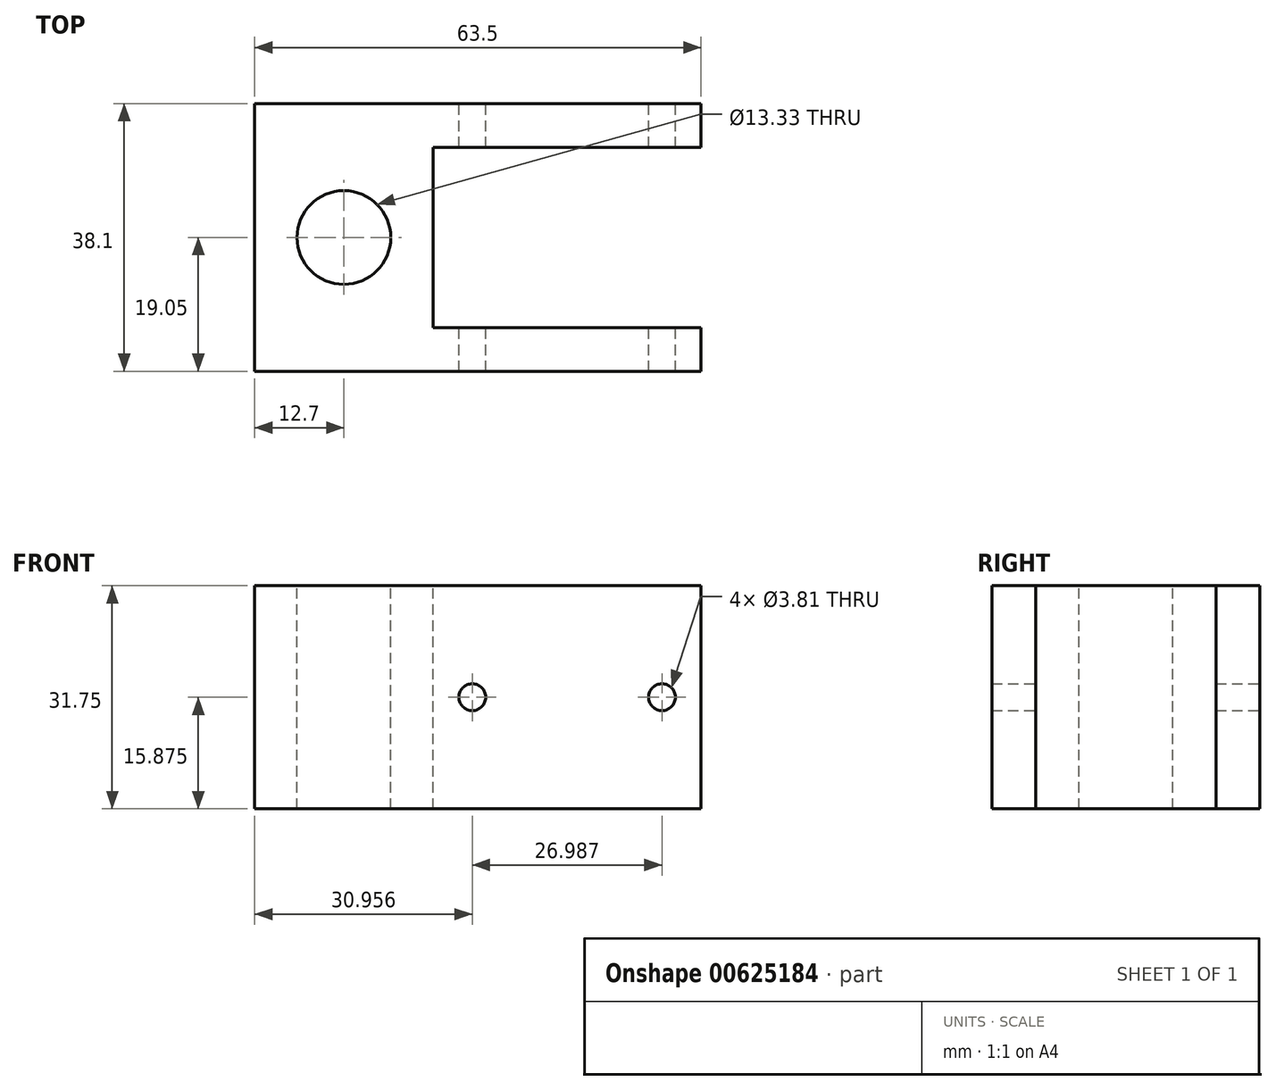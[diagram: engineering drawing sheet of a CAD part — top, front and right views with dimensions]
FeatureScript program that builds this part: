
annotation { "Feature Type Name" : "Feature", "Feature Type Description" : "" }
export const myFeature = defineFeature(function(context is Context, id is Id, definition is map)
    precondition{}
    {
        {
            var Q0;
            Q0=qCreatedBy(makeId("Top.planeOp"),FACE);
            var sketch = newSketch(context, id + "F0", { "sketchPlane" : qUnion([Q0])});
            skLineSegment(sketch, "E0.bottom", {"start": v(12.7, -19.05) * mm, "end": v(-12.7, -19.05) * mm});
            skLineSegment(sketch, "E0.top", {"start": v(12.7, 19.05) * mm, "end": v(-12.7, 19.05) * mm});
            skLineSegment(sketch, "E0.left", {"start": v(12.7, -19.05) * mm, "end": v(12.7, 19.05) * mm});
            skLineSegment(sketch, "E0.right", {"start": v(-12.7, -19.05) * mm, "end": v(-12.7, 19.05) * mm});
            skPoint(sketch, "E0.middle", {"position": v(0, 0) * mm});
            skSolve(sketch);
        }
        {
            var Q0;
            Q0=makeQuery(id+"F0.imprint","IMPRINT",FACE,{"disambiguationData":[TD([[makeQuery(id+"F0.imprint","IMPRINT",EDGE,{"derivedFrom":sQuery(id+"F0.wireOp",EDGE,"E0.bottom")}),-1.0]])]});
            extrude(context, id + "F1", {"entities" : qUnion([Q0]), "depth" : 31.75 * mm, "offsetDistance" : 25.4 * mm});
        }
        {
            var Q0;
            Q0=makeQuery(id+"F1.opExtrude","SWEPT_FACE",FACE,{"disambiguationData":[OSD([sQuery(id+"F0.wireOp",EDGE,"E0.left")])]});
            var sketch = newSketch(context, id + "F2", { "sketchPlane" : qUnion([Q0])});
            skLineSegment(sketch, "E1.bottom", {"start": v(-19.05, 0) * mm, "end": v(-12.83, 0) * mm});
            skLineSegment(sketch, "E1.top", {"start": v(-19.05, 31.75) * mm, "end": v(-12.83, 31.75) * mm});
            skLineSegment(sketch, "E1.left", {"start": v(-19.05, 0) * mm, "end": v(-19.05, 31.75) * mm});
            skLineSegment(sketch, "E1.right", {"start": v(-12.83, 0) * mm, "end": v(-12.83, 31.75) * mm});
            skLineSegment(sketch, "E2.bottom", {"start": v(19.05, 0) * mm, "end": v(12.83, 0) * mm});
            skLineSegment(sketch, "E2.top", {"start": v(19.05, 31.75) * mm, "end": v(12.83, 31.75) * mm});
            skLineSegment(sketch, "E2.left", {"start": v(19.05, 0) * mm, "end": v(19.05, 31.75) * mm});
            skLineSegment(sketch, "E2.right", {"start": v(12.83, 0) * mm, "end": v(12.83, 31.75) * mm});
            skSolve(sketch);
        }
        {
            var Q0;
            Q0 = qSketchRegion(id + "F2", true);
            extrude(context, id + "F3", {"entities" : qUnion([Q0]), "operationType" : NewBodyOperationType.ADD, "depth" : 38.1 * mm, "offsetDistance" : 25.4 * mm});
        }
        {
            var Q0;
            Q0=makeQuery(id+"F3.boolean.opBoolean","MERGE",FACE,{"derivedFrom":[makeQuery(id+"F1.opExtrude","CAP_FACE",FACE,{"disambiguationData":[OSD([sQuery(id+"F0.wireOp",EDGE,"E0.bottom"),sQuery(id+"F0.wireOp",EDGE,"E0.top"),sQuery(id+"F0.wireOp",EDGE,"E0.left"),sQuery(id+"F0.wireOp",EDGE,"E0.right")])],"isStart":false}),makeQuery(id+"F3.opExtrude","SWEPT_FACE",FACE,{"disambiguationData":[OSD([sQuery(id+"F2.wireOp",EDGE,"E1.top")])]}),makeQuery(id+"F3.opExtrude","SWEPT_FACE",FACE,{"disambiguationData":[OSD([sQuery(id+"F2.wireOp",EDGE,"E2.top")])]})]});
            var sketch = newSketch(context, id + "F4", { "sketchPlane" : qUnion([Q0])});
            skCircle(sketch, "E3", {"center": v(0, 0) * mm, "radius": 6.67 * mm});
            skSolve(sketch);
        }
        {
            var Q0;
            Q0 = qSketchRegion(id + "F4", true);
            extrude(context, id + "F5", {"entities" : qUnion([Q0]), "operationType" : NewBodyOperationType.REMOVE, "endBound" : BoundingType.THROUGH_ALL, "oppositeDirection" : true, "depth" : 25.4 * mm, "offsetDistance" : 25.4 * mm});
        }
        {
            var Q0;
            Q0=makeQuery(id+"F3.boolean.opBoolean","MERGE",FACE,{"derivedFrom":[makeQuery(id+"F1.opExtrude","SWEPT_FACE",FACE,{"disambiguationData":[OSD([sQuery(id+"F0.wireOp",EDGE,"E0.top")])]}),makeQuery(id+"F3.opExtrude","SWEPT_FACE",FACE,{"disambiguationData":[OSD([sQuery(id+"F2.wireOp",EDGE,"E2.left")])]})]});
            var sketch = newSketch(context, id + "F6", { "sketchPlane" : qUnion([Q0])});
            skCircle(sketch, "E4", {"center": v(-45.24, 15.88) * mm, "radius": 1.9 * mm});
            skCircle(sketch, "E5", {"center": v(-18.26, 15.88) * mm, "radius": 1.9 * mm});
            skSolve(sketch);
        }
        {
            var Q0;
            Q0 = qSketchRegion(id + "F6", true);
            extrude(context, id + "F7", {"entities" : qUnion([Q0]), "operationType" : NewBodyOperationType.REMOVE, "endBound" : BoundingType.THROUGH_ALL, "oppositeDirection" : true, "depth" : 25.4 * mm, "offsetDistance" : 25.4 * mm});
        }
    });
